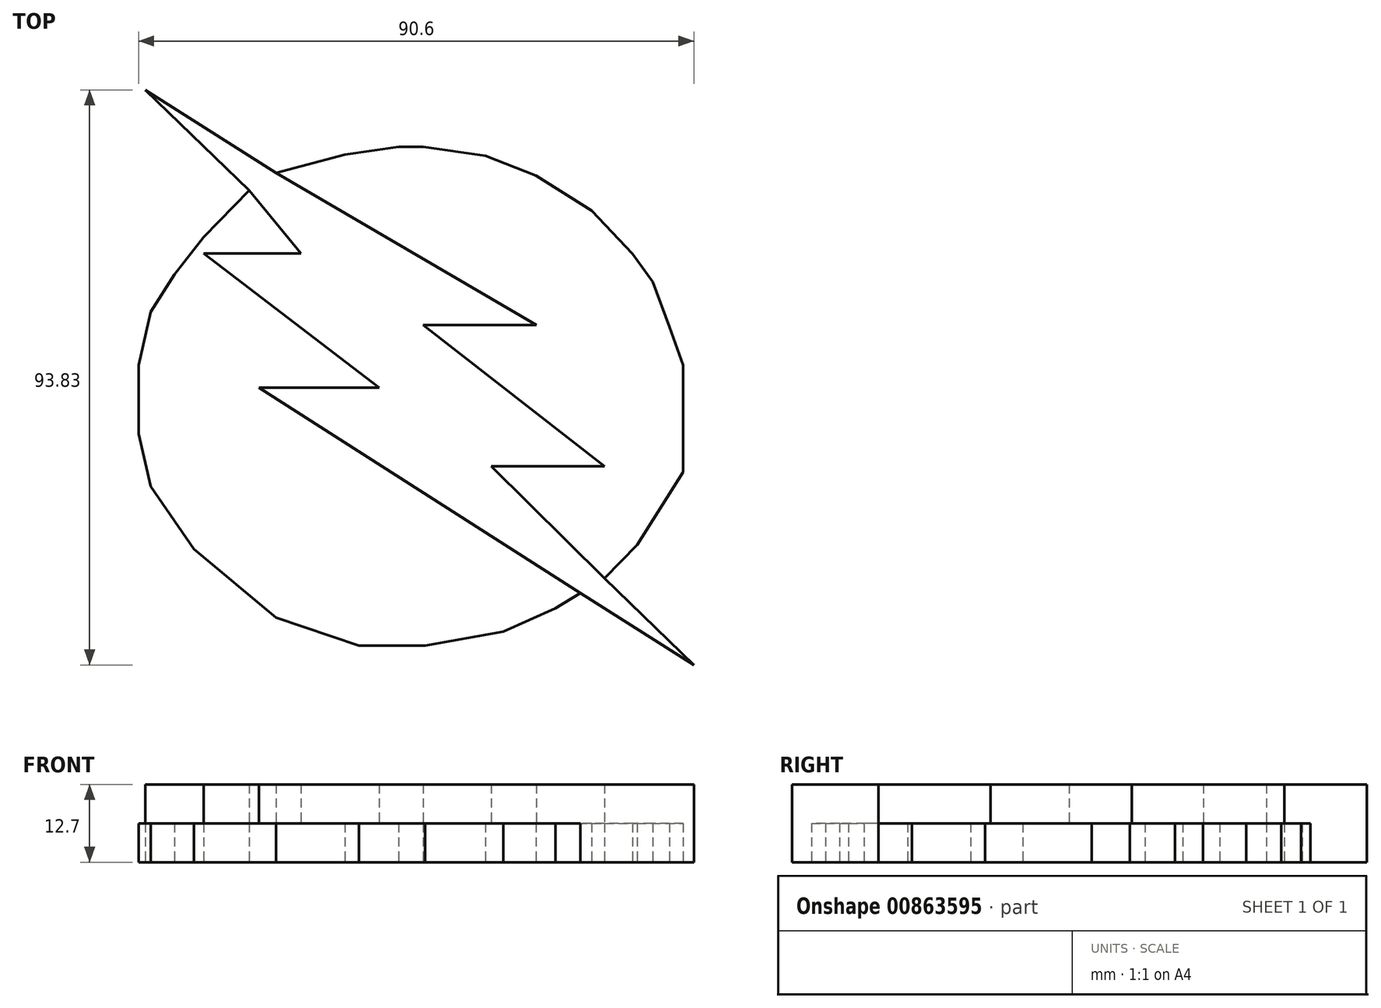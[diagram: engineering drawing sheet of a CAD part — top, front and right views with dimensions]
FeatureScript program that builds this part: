
annotation { "Feature Type Name" : "Feature", "Feature Type Description" : "" }
export const myFeature = defineFeature(function(context is Context, id is Id, definition is map)
    precondition{}
    {
        {
            var Q0;
            Q0=qCreatedBy(makeId("Top.planeOp"),FACE);
            var sketch = newSketch(context, id + "F0", { "sketchPlane" : qUnion([Q0])});
            skLineSegment(sketch, "E0", {"start": v(0, 41.2) * mm, "end": v(-8.74, 39.88) * mm});
            skLineSegment(sketch, "E1", {"start": v(-8.74, 39.88) * mm, "end": v(-20.02, 36.94) * mm});
            skLineSegment(sketch, "E2", {"start": v(-20.02, 36.94) * mm, "end": v(-41.33, 50.45) * mm});
            skLineSegment(sketch, "E3", {"start": v(-41.33, 50.45) * mm, "end": v(-24.4, 34.04) * mm});
            skLineSegment(sketch, "E4", {"start": v(-24.4, 34.04) * mm, "end": v(-31.8, 26.41) * mm});
            skLineSegment(sketch, "E5", {"start": v(-31.8, 26.41) * mm, "end": v(-36.55, 20.37) * mm});
            skLineSegment(sketch, "E6", {"start": v(-36.55, 20.37) * mm, "end": v(-40.45, 14.22) * mm});
            skLineSegment(sketch, "E7", {"start": v(-40.45, 14.22) * mm, "end": v(-42.42, 5.56) * mm});
            skLineSegment(sketch, "E8", {"start": v(-42.42, 5.56) * mm, "end": v(-42.42, -5.72) * mm});
            skLineSegment(sketch, "E9", {"start": v(-42.42, -5.72) * mm, "end": v(-40.45, -14.24) * mm});
            skLineSegment(sketch, "E10", {"start": v(-40.45, -14.24) * mm, "end": v(-33.43, -24.52) * mm});
            skLineSegment(sketch, "E11", {"start": v(-33.43, -24.52) * mm, "end": v(-20.02, -35.63) * mm});
            skLineSegment(sketch, "E12", {"start": v(-20.02, -35.63) * mm, "end": v(-6.46, -40.2) * mm});
            skLineSegment(sketch, "E13", {"start": v(-6.46, -40.2) * mm, "end": v(4.33, -40.2) * mm});
            skLineSegment(sketch, "E14", {"start": v(4.33, -40.2) * mm, "end": v(17.08, -37.92) * mm});
            skLineSegment(sketch, "E15", {"start": v(17.08, -37.92) * mm, "end": v(25.58, -34.16) * mm});
            skLineSegment(sketch, "E16", {"start": v(25.58, -34.16) * mm, "end": v(29.67, -31.64) * mm});
            skLineSegment(sketch, "E17", {"start": v(29.67, -31.64) * mm, "end": v(48.18, -43.38) * mm});
            skLineSegment(sketch, "E18", {"start": v(48.18, -43.38) * mm, "end": v(33.59, -29.26) * mm});
            skLineSegment(sketch, "E19", {"start": v(33.59, -29.26) * mm, "end": v(38.9, -23.78) * mm});
            skLineSegment(sketch, "E20", {"start": v(38.9, -23.78) * mm, "end": v(42.24, -18.5) * mm});
            skLineSegment(sketch, "E21", {"start": v(42.24, -18.5) * mm, "end": v(46.44, -11.88) * mm});
            skLineSegment(sketch, "E22", {"start": v(46.44, -11.88) * mm, "end": v(46.44, -3.68) * mm});
            skLineSegment(sketch, "E23", {"start": v(46.44, -3.68) * mm, "end": v(46.44, 5.56) * mm});
            skLineSegment(sketch, "E24", {"start": v(46.44, 5.56) * mm, "end": v(44.21, 11.77) * mm});
            skLineSegment(sketch, "E25", {"start": v(44.21, 11.77) * mm, "end": v(41.44, 19.12) * mm});
            skLineSegment(sketch, "E26", {"start": v(41.44, 19.12) * mm, "end": v(38.17, 23.7) * mm});
            skLineSegment(sketch, "E27", {"start": v(38.17, 23.7) * mm, "end": v(31.46, 30.73) * mm});
            skLineSegment(sketch, "E28", {"start": v(31.46, 30.73) * mm, "end": v(22.43, 36.46) * mm});
            skLineSegment(sketch, "E29", {"start": v(22.43, 36.46) * mm, "end": v(14.14, 39.72) * mm});
            skLineSegment(sketch, "E30", {"start": v(14.14, 39.72) * mm, "end": v(4, 41.2) * mm});
            skLineSegment(sketch, "E31", {"start": v(4, 41.2) * mm, "end": v(0, 41.2) * mm});
            skLineSegment(sketch, "E32", {"start": v(-24.4, 34.04) * mm, "end": v(-15.94, 23.77) * mm});
            skLineSegment(sketch, "E33", {"start": v(-15.94, 23.77) * mm, "end": v(-31.8, 23.77) * mm});
            skLineSegment(sketch, "E34", {"start": v(-3.19, 1.87) * mm, "end": v(-22.8, 1.87) * mm});
            skLineSegment(sketch, "E35", {"start": v(-22.8, 1.87) * mm, "end": v(29.67, -31.64) * mm});
            skLineSegment(sketch, "E36", {"start": v(-20.02, 36.94) * mm, "end": v(22.47, 12.1) * mm});
            skLineSegment(sketch, "E37", {"start": v(22.47, 12.1) * mm, "end": v(4, 12.1) * mm});
            skLineSegment(sketch, "E38", {"start": v(4, 12.1) * mm, "end": v(33.59, -10.95) * mm});
            skLineSegment(sketch, "E39", {"start": v(33.59, -10.95) * mm, "end": v(15.12, -10.95) * mm});
            skLineSegment(sketch, "E40", {"start": v(15.12, -10.95) * mm, "end": v(33.59, -29.26) * mm});
            skLineSegment(sketch, "E41", {"start": v(-31.8, 23.77) * mm, "end": v(-3.19, 1.87) * mm});
            skSolve(sketch);
        }
        {
            var Q0;
            Q0=makeQuery(id+"F0.imprint","IMPRINT",FACE,{"disambiguationData":[TD([[makeQuery(id+"F0.imprint","IMPRINT",EDGE,{"derivedFrom":sQuery(id+"F0.wireOp",EDGE,"E2")}),1.0]])]});
            extrude(context, id + "F1", {"entities" : qUnion([Q0]), "depth" : 12.7 * mm, "offsetDistance" : 25.4 * mm});
        }
        {
            var Q0;
            Q0 = qSketchRegion(id + "F0", true);
            extrude(context, id + "F2", {"entities" : qUnion([Q0]), "operationType" : NewBodyOperationType.ADD, "depth" : 6.35 * mm, "offsetDistance" : 25.4 * mm});
        }
    });
